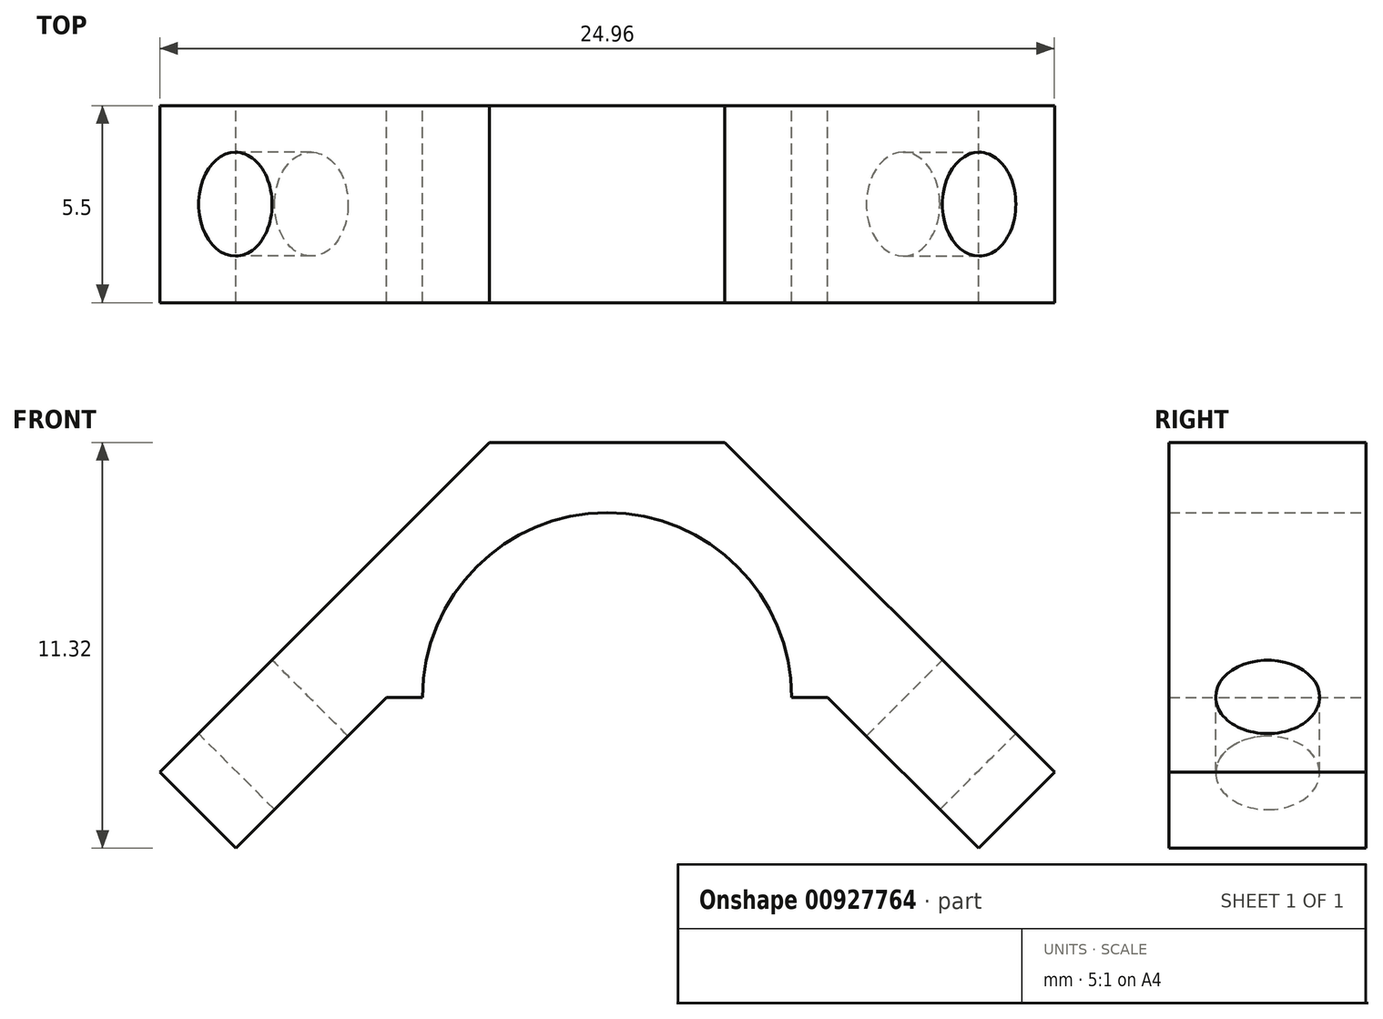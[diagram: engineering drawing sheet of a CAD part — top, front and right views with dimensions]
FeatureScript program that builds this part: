
annotation { "Feature Type Name" : "Feature", "Feature Type Description" : "" }
export const myFeature = defineFeature(function(context is Context, id is Id, definition is map)
    precondition{}
    {
        {
            var Q0;
            Q0=qCreatedBy(makeId("Front.planeOp"),FACE);
            var sketch = newSketch(context, id + "F0", { "sketchPlane" : qUnion([Q0])});
            skArc(sketch, "E0", {"start": v(5.15, 0) * mm, "mid": v(0, 5.15) * mm, "end": v(-5.15, 0) * mm});
            skLineSegment(sketch, "E1", {"start": v(-5.15, 0) * mm, "end": v(-6.15, 0) * mm});
            skLineSegment(sketch, "E2", {"start": v(-6.15, 0) * mm, "end": v(-5.15, 0) * mm});
            skLineSegment(sketch, "E3", {"start": v(6.15, 0) * mm, "end": v(10.36, -4.21) * mm});
            skLineSegment(sketch, "E4", {"start": v(-6.15, 0) * mm, "end": v(-10.36, -4.21) * mm});
            skLineSegment(sketch, "E5.trimOffspring", {"start": v(5.15, 0) * mm, "end": v(6.15, 0) * mm});
            skLineSegment(sketch, "E6", {"start": v(-10.36, -4.21) * mm, "end": v(-12.48, -2.1) * mm});
            skLineSegment(sketch, "E7", {"start": v(-12.48, -2.1) * mm, "end": v(-3.28, 7.11) * mm});
            skLineSegment(sketch, "E8", {"start": v(10.36, -4.21) * mm, "end": v(12.48, -2.1) * mm});
            skLineSegment(sketch, "E9", {"start": v(12.48, -2.1) * mm, "end": v(3.28, 7.11) * mm});
            skLineSegment(sketch, "E10", {"start": v(-3.28, 7.11) * mm, "end": v(3.28, 7.11) * mm});
            skSolve(sketch);
        }
        {
            var Q0;
            Q0=makeQuery(id+"F0.imprint","IMPRINT",FACE,{"disambiguationData":[TD([[makeQuery(id+"F0.imprint","IMPRINT",EDGE,{"derivedFrom":sQuery(id+"F0.wireOp",EDGE,"E0")}),-1.0]])]});
            extrude(context, id + "F1", {"entities" : qUnion([Q0]), "depth" : 5.5 * mm, "offsetDistance" : 25 * mm});
        }
        {
            var Q0;
            Q0=makeQuery(id+"F1.opExtrude","SWEPT_FACE",FACE,{"disambiguationData":[OSD([sQuery(id+"F0.wireOp",EDGE,"E7")])]});
            var sketch = newSketch(context, id + "F2", { "sketchPlane" : qUnion([Q0])});
            skLineSegment(sketch, "E11", {"start": v(0, -10.3) * mm, "end": v(0, -4.35) * mm});
            skLineSegment(sketch, "E12", {"start": v(0, -4.35) * mm, "end": v(5.5, -4.35) * mm});
            skLineSegment(sketch, "E13", {"start": v(2.75, -4.35) * mm, "end": v(2.75, -10.3) * mm, "construction": true});
            skLineSegment(sketch, "E14", {"start": v(0, -7.33) * mm, "end": v(5.5, -7.33) * mm, "construction": true});
            skPoint(sketch, "E14.endSnap0", {"position": v(2.75, -7.33) * mm});
            skCircle(sketch, "E15", {"center": v(2.75, -7.33) * mm, "radius": 1.45 * mm});
            skSolve(sketch);
        }
        {
            var Q0;
            Q0=makeQuery(id+"F2.imprint","IMPRINT",FACE,{"disambiguationData":[TD([[makeQuery(id+"F2.imprint","IMPRINT",EDGE,{"derivedFrom":sQuery(id+"F2.wireOp",EDGE,"E15")}),1.0]])]});
            extrude(context, id + "F3", {"entities" : qUnion([Q0]), "operationType" : NewBodyOperationType.REMOVE, "oppositeDirection" : true, "depth" : 25 * mm, "offsetDistance" : 25 * mm});
        }
        {
            var Q0;
            Q0=makeQuery(id+"F1.opExtrude","SWEPT_FACE",FACE,{"disambiguationData":[OSD([sQuery(id+"F0.wireOp",EDGE,"E9")])]});
            var sketch = newSketch(context, id + "F4", { "sketchPlane" : qUnion([Q0])});
            skLineSegment(sketch, "E16", {"start": v(-5.5, -10.3) * mm, "end": v(-5.5, -4.35) * mm});
            skLineSegment(sketch, "E17", {"start": v(-5.5, -4.35) * mm, "end": v(0, -4.35) * mm});
            skLineSegment(sketch, "E18", {"start": v(-2.75, -4.35) * mm, "end": v(-2.75, -10.3) * mm, "construction": true});
            skLineSegment(sketch, "E19", {"start": v(-5.5, -7.33) * mm, "end": v(0, -7.33) * mm, "construction": true});
            skPoint(sketch, "E19.endSnap0", {"position": v(-2.75, -7.33) * mm});
            skCircle(sketch, "E20", {"center": v(-2.75, -7.33) * mm, "radius": 1.45 * mm});
            skSolve(sketch);
        }
        {
            var Q0;
            Q0=makeQuery(id+"F4.imprint","IMPRINT",FACE,{"disambiguationData":[TD([[makeQuery(id+"F4.imprint","IMPRINT",EDGE,{"derivedFrom":sQuery(id+"F4.wireOp",EDGE,"E20")}),1.0]])]});
            extrude(context, id + "F5", {"entities" : qUnion([Q0]), "operationType" : NewBodyOperationType.REMOVE, "oppositeDirection" : true, "depth" : 25 * mm, "offsetDistance" : 25 * mm});
        }
    });
